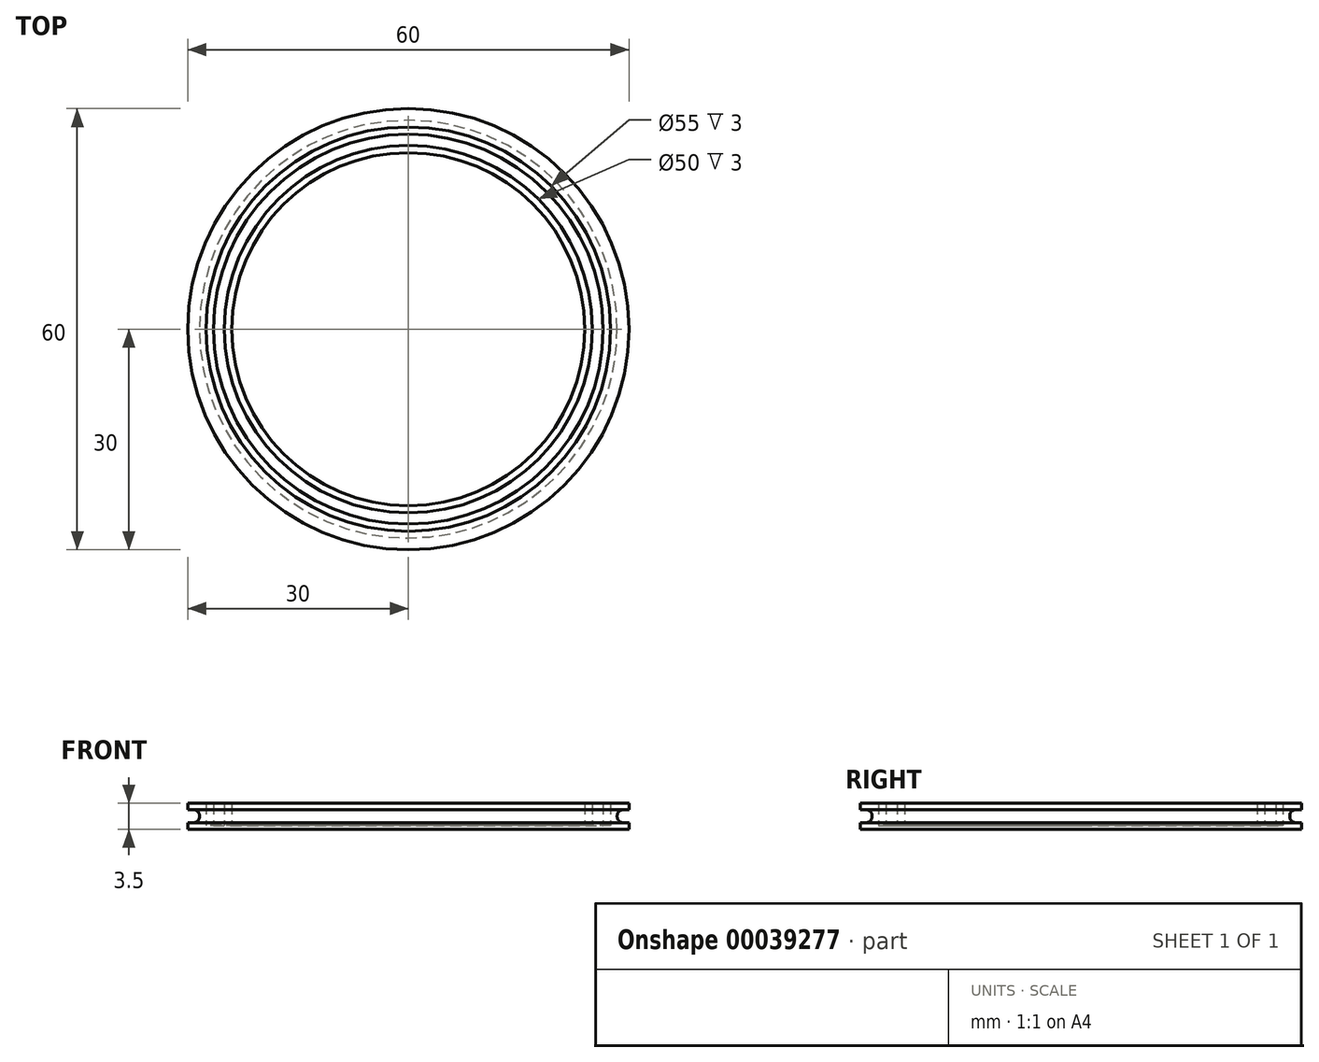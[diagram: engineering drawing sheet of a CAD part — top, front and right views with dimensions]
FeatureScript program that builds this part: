
annotation { "Feature Type Name" : "Feature", "Feature Type Description" : "" }
export const myFeature = defineFeature(function(context is Context, id is Id, definition is map)
    precondition{}
    {
        {
            var Q0;
            Q0=qCreatedBy(makeId("Top.planeOp"),FACE);
            var sketch = newSketch(context, id + "F0", { "sketchPlane" : qUnion([Q0])});
            skCircle(sketch, "E0", {"center": v(0, 0) * mm, "radius": 30 * mm});
            skCircle(sketch, "E1", {"center": v(0, 0) * mm, "radius": 27.5 * mm});
            skCircle(sketch, "E2", {"center": v(0, 0) * mm, "radius": 25 * mm});
            skCircle(sketch, "E3.0", {"center": v(0, 0) * mm, "radius": 24 * mm});
            skCircle(sketch, "E4.0", {"center": v(0, 0) * mm, "radius": 26.5 * mm});
            skSolve(sketch);
        }
        {
            var Q0;
            Q0=makeQuery(id+"F0.imprint","IMPRINT",FACE,{"disambiguationData":[TD([[makeQuery(id+"F0.imprint","IMPRINT",EDGE,{"derivedFrom":sQuery(id+"F0.wireOp",EDGE,"E0")}),1.0]])]});
            var Q1;
            Q1=makeQuery(id+"F0.imprint","IMPRINT",FACE,{"disambiguationData":[TD([[makeQuery(id+"F0.imprint","IMPRINT",EDGE,{"derivedFrom":sQuery(id+"F0.wireOp",EDGE,"E2")}),-1.0]])]});
            var Q2;
            Q2=makeQuery(id+"F0.imprint","IMPRINT",FACE,{"disambiguationData":[TD([[makeQuery(id+"F0.imprint","IMPRINT",EDGE,{"derivedFrom":sQuery(id+"F0.wireOp",EDGE,"E3.0")}),1.0]])]});
            extrude(context, id + "F1", {"entities" : qUnion([Q0, Q1, Q2]), "depth" : 3 * mm});
        }
        {
            var Q0;
            Q0=makeQuery(id+"F1.opExtrude","CAP_FACE",FACE,{"disambiguationData":[OSD([sQuery(id+"F0.wireOp",EDGE,"E1")])],"isStart":true});
            var sketch = newSketch(context, id + "F2", { "sketchPlane" : qUnion([Q0])});
            skCircle(sketch, "E5", {"center": v(0, 0) * mm, "radius": 30 * mm});
            skSolve(sketch);
        }
        {
            var Q0;
            Q0=qSketchRegion(id+"F2",true);
            extrude(context, id + "F3", {"entities" : qUnion([Q0]), "operationType" : NewBodyOperationType.ADD, "depth" : .5 * mm});
        }
        {
            var Q0;
            Q0=qCreatedBy(makeId("Front.planeOp"),FACE);
            var sketch = newSketch(context, id + "F4", { "sketchPlane" : qUnion([Q0])});
            skLineSegment(sketch, "E6", {"start": v(30, 2.89) * mm, "end": v(30, 1.26) * mm, "construction": true});
            skLineSegment(sketch, "E7", {"start": v(30, 1.26) * mm, "end": v(30, -0.38) * mm, "construction": true});
            skLineSegment(sketch, "E8.bottom", {"start": v(30, 0.38) * mm, "end": v(29.2, 0.38) * mm});
            skLineSegment(sketch, "E8.top", {"start": v(30, 2.13) * mm, "end": v(29.2, 2.13) * mm});
            skLineSegment(sketch, "E8.left", {"start": v(30, 0.38) * mm, "end": v(30, 2.13) * mm, "construction": true});
            skLineSegment(sketch, "E8.right", {"start": v(28.4, 1.18) * mm, "end": v(28.4, 1.33) * mm});
            skLineSegment(sketch, "E9", {"start": v(30, 1.26) * mm, "end": v(28.4, 1.26) * mm, "construction": true});
            skPoint(sketch, "E10.visualSharp", {"position": v(28.4, 2.13) * mm});
            skArc(sketch, "E10.filletArc", {"start": v(29.2, 2.13) * mm, "mid": v(28.63, 1.9) * mm, "end": v(28.4, 1.33) * mm});
            skPoint(sketch, "E11.visualSharp", {"position": v(28.4, 0.38) * mm});
            skArc(sketch, "E11.filletArc", {"start": v(28.4, 1.18) * mm, "mid": v(28.63, 0.62) * mm, "end": v(29.2, 0.38) * mm});
            skArc(sketch, "E12", {"start": v(30, 2.13) * mm, "mid": v(29.13, 1.26) * mm, "end": v(30, 0.38) * mm, "construction": true});
            skArc(sketch, "E13", {"start": v(30, 0.38) * mm, "mid": v(30.88, 1.26) * mm, "end": v(30, 2.13) * mm});
            skSolve(sketch);
        }
        {
            var Q0;
            Q0 = qSketchRegion(id + "F4", true);
            var Q1;
            Q1=makeQuery(id+"F3.boolean.opBoolean","MERGE",FACE,{"derivedFrom":[makeQuery(id+"F1.opExtrude","SWEPT_FACE",FACE,{"disambiguationData":[OSD([sQuery(id+"F0.wireOp",EDGE,"E0")])]}),makeQuery(id+"F3.opExtrude","SWEPT_FACE",FACE,{"disambiguationData":[OSD([sQuery(id+"F2.wireOp",EDGE,"E5")])]})]});
            revolve(context, id + "F5", {"operationType" : NewBodyOperationType.REMOVE, "entities" : qUnion([Q0]), "axis" : qUnion([Q1]), "revolveType" : RevolveType.FULL, "oppositeDirection" : true});
        }
    });
